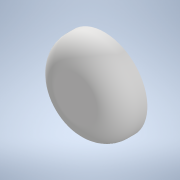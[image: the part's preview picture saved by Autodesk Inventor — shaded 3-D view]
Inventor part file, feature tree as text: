
AUTODESK INVENTOR PART (.ipt)
format: ipt  version: 2020.2 (Build 242310000, 310)  size: 123,392 bytes
history: native  units: in
note: dims shown in document units (in); Inventor stores cm internally (conversion verified against a paired STEP export)
features: revolve x1, fillet x1, sketch x1
ambient origin geometry x8: Origin, YZ Plane, XZ Plane, XY Plane, X Axis, Y Axis, Z Axis, Center Point
bodies: Solid1 (feature_tree)
feature tree (3):
  revolve  "Revolution1"  [1 undecoded]
  fillet  "Fillet1"  [1 undecoded]
  sketch  "Sketch1"  dims[d0=1.1811in d1=0.7874in d2=90.0deg d3=0.5906in]
note: 2 required parameter values undecoded (feature->parameter linkage not recoverable at this tier; creation-order binding heuristic only, values carry confidence <= 0.55)